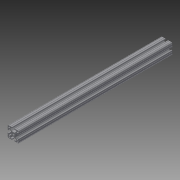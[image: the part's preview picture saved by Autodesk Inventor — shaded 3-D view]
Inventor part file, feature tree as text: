
AUTODESK INVENTOR PART (.ipt)
format: ipt  version: 2013 (Build 170138000, 138)  size: 286,720 bytes
history: native  units: in
note: dims shown in document units (in); Inventor stores cm internally (conversion verified against a paired STEP export)
features: extrude x1, sketch x1
ambient origin geometry x8: Origin, YZ Plane, XZ Plane, XY Plane, X Axis, Y Axis, Z Axis, Center Point
bodies: Solid1 (feature_tree)
feature tree (2):
  extrude  "Extrusion1"  [1 undecoded]
  sketch  "Sketch1"  dims[d0=20.75in d1=0.0in]
note: 1 required parameter value undecoded (feature->parameter linkage not recoverable at this tier; creation-order binding heuristic only, values carry confidence <= 0.55)
